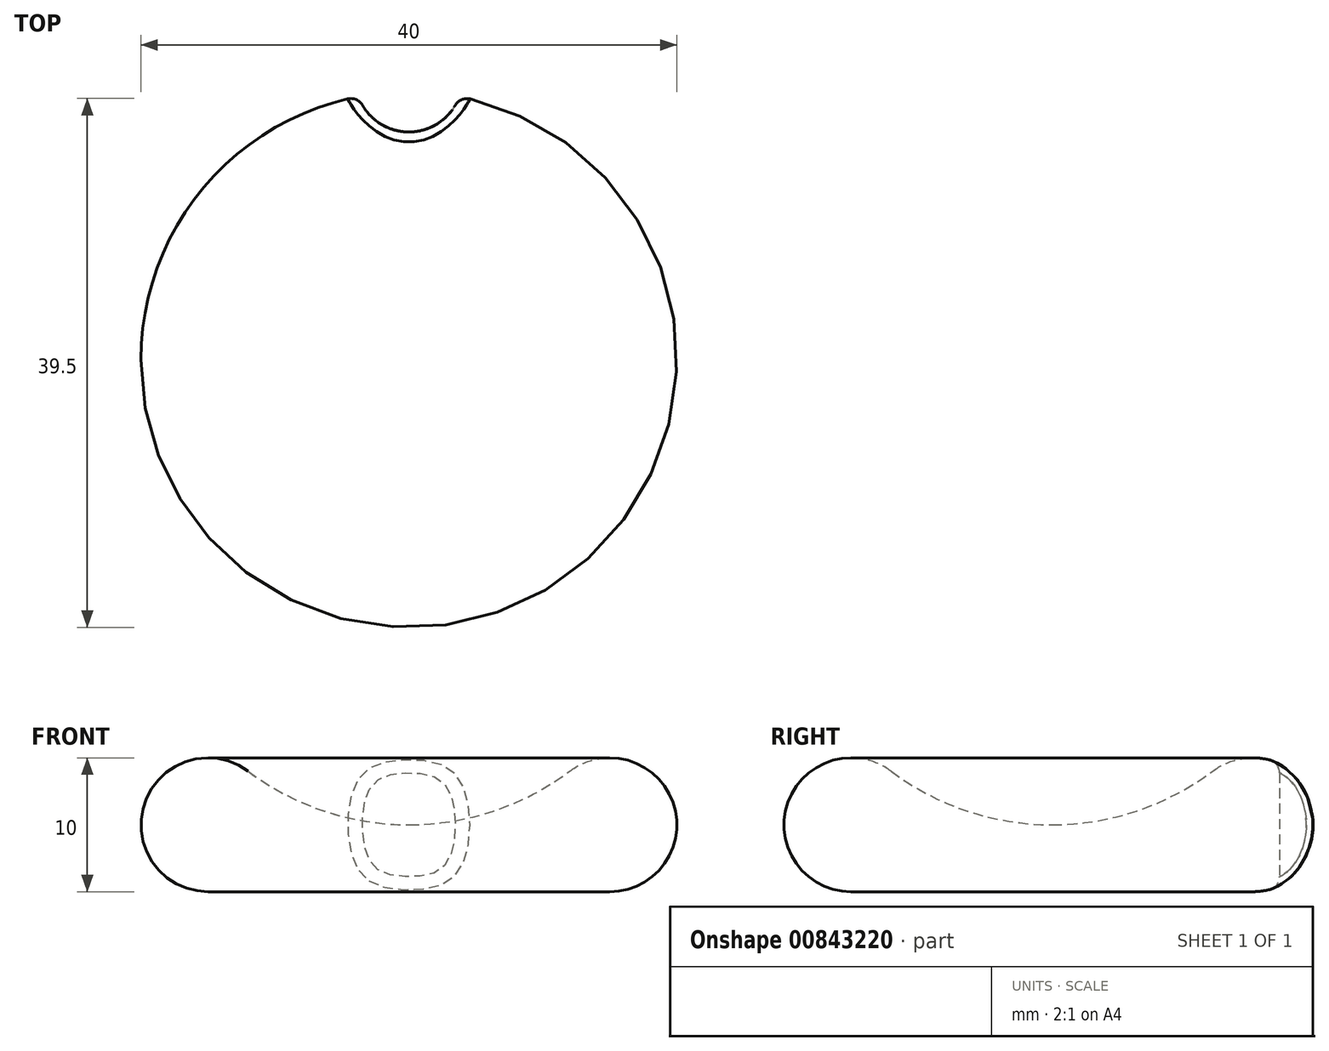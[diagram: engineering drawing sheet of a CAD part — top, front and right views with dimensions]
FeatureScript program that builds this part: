
annotation { "Feature Type Name" : "Feature", "Feature Type Description" : "" }
export const myFeature = defineFeature(function(context is Context, id is Id, definition is map)
    precondition{}
    {
        {
            var Q0;
            Q0=qCreatedBy(makeId("Front.planeOp"),FACE);
            var sketch = newSketch(context, id + "F0", { "sketchPlane" : qUnion([Q0])});
            skArc(sketch, "E0", {"start": v(-12, 9) * mm, "mid": v(-19.74, 6.58) * mm, "end": v(-15, 0) * mm});
            skArc(sketch, "E1", {"start": v(-12, 9) * mm, "mid": v(-6.32, 6.03) * mm, "end": v(0, 5) * mm});
            skLineSegment(sketch, "E2", {"start": v(-15, 0) * mm, "end": v(0, 0) * mm});
            skLineSegment(sketch, "E3", {"start": v(0, 0) * mm, "end": v(0, 5) * mm});
            skSolve(sketch);
        }
        {
            var Q0;
            Q0=makeQuery(id+"F0.imprint","IMPRINT",FACE,{"disambiguationData":[TD([[makeQuery(id+"F0.imprint","IMPRINT",EDGE,{"derivedFrom":sQuery(id+"F0.wireOp",EDGE,"E0")}),1.0]])]});
            var Q1;
            Q1=sQuery(id+"F0.wireOp",EDGE,"E3");
            revolve(context, id + "F1", {"surfaceOperationType" : NewSurfaceOperationType.NEW, "entities" : qUnion([Q0]), "axis" : qUnion([Q1]), "revolveType" : RevolveType.FULL});
        }
        {
            var Q0;
            Q0=qCreatedBy(makeId("Top.planeOp"),FACE);
            var sketch = newSketch(context, id + "F2", { "sketchPlane" : qUnion([Q0])});
            skCircle(sketch, "E4", {"center": v(0, 21) * mm, "radius": 4 * mm});
            skSolve(sketch);
        }
        {
            var Q0;
            Q0=makeQuery(id+"F2.imprint","IMPRINT",FACE,{"disambiguationData":[TD([[makeQuery(id+"F2.imprint","IMPRINT",EDGE,{"derivedFrom":sQuery(id+"F2.wireOp",EDGE,"E4")}),1.0]])]});
            extrude(context, id + "F3", {"entities" : qUnion([Q0]), "operationType" : NewBodyOperationType.REMOVE, "depth" : 25 * mm, "offsetDistance" : 25 * mm});
        }
        {
            var Q0;
            Q0=makeQuery(id+"F3.boolean.opBoolean","INTERSECT",EDGE,{"derivedFrom":[makeQuery(id+"F1.opRevolve","SWEPT_FACE",FACE,{"disambiguationData":[OSD([sQuery(id+"F0.wireOp",EDGE,"E0")])]}),makeQuery(id+"F3.opExtrude","SWEPT_FACE",FACE,{"disambiguationData":[OSD([sQuery(id+"F2.wireOp",EDGE,"E4")])]})]});
            fillet(context, id + "F4", {"entities" : qUnion([Q0]), "radius" : 1 * mm, "tangentPropagation" : true, "allowEdgeOverflow" : false});
        }
    });
